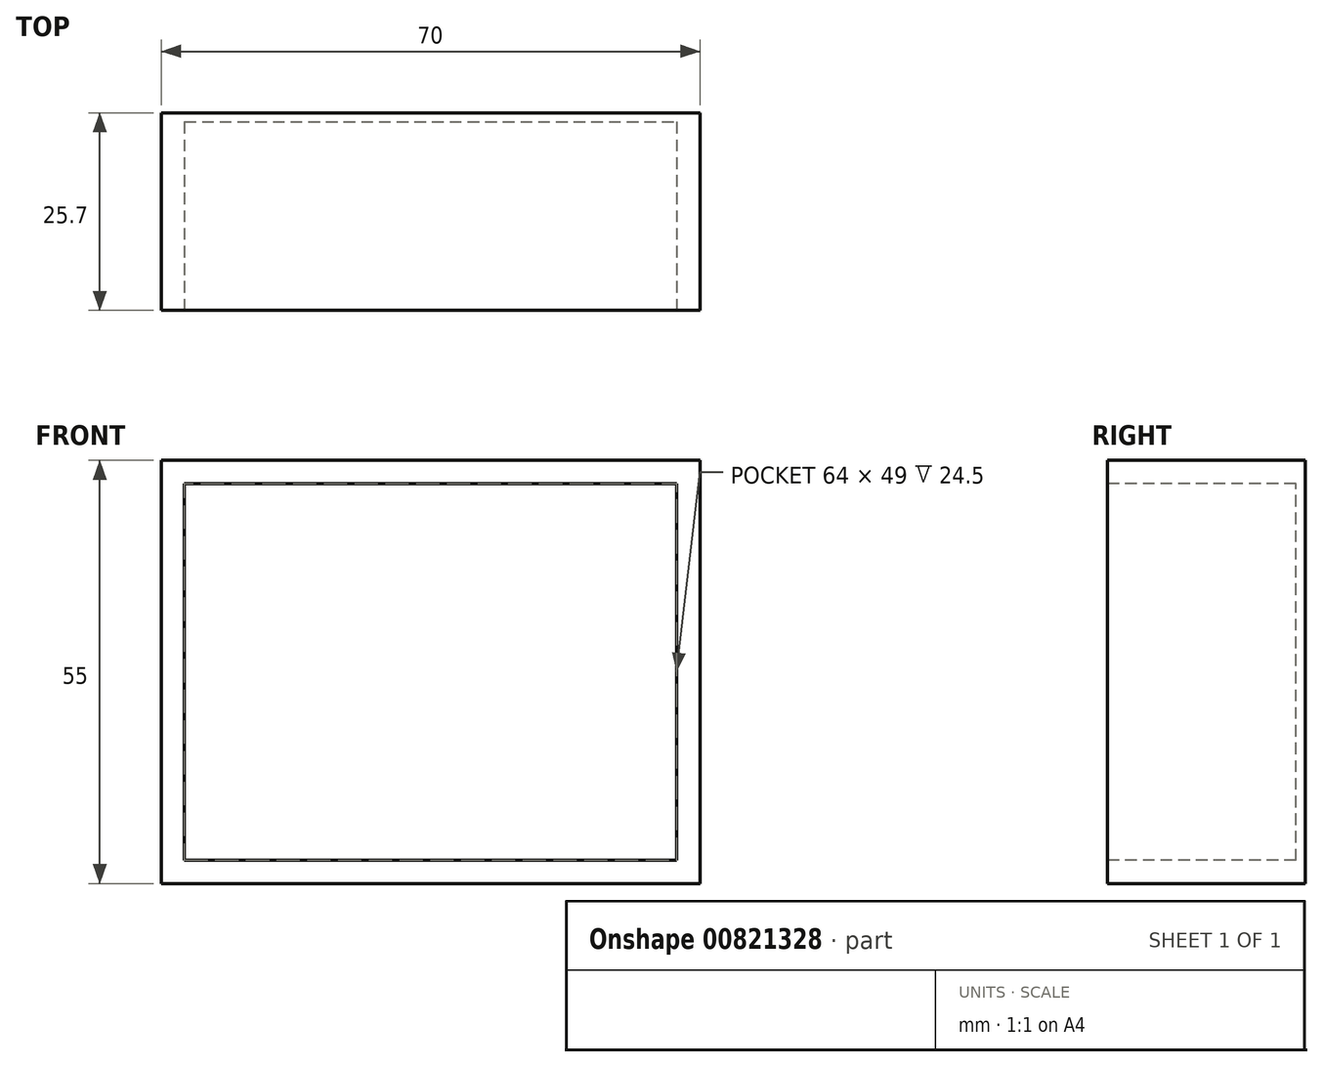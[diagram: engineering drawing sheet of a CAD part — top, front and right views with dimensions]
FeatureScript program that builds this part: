
annotation { "Feature Type Name" : "Feature", "Feature Type Description" : "" }
export const myFeature = defineFeature(function(context is Context, id is Id, definition is map)
    precondition{}
    {
        {
            var Q0;
            Q0=qCreatedBy(makeId("Front.planeOp"),FACE);
            var sketch = newSketch(context, id + "F0", { "sketchPlane" : qUnion([Q0])});
            skLineSegment(sketch, "E0.bottom", {"start": v(0, 0) * mm, "end": v(70, 0) * mm});
            skLineSegment(sketch, "E0.top", {"start": v(0, 55) * mm, "end": v(70, 55) * mm});
            skLineSegment(sketch, "E0.left", {"start": v(0, 0) * mm, "end": v(0, 55) * mm});
            skLineSegment(sketch, "E0.right", {"start": v(70, 0) * mm, "end": v(70, 55) * mm});
            skSolve(sketch);
        }
        {
            var Q0;
            Q0=makeQuery(id+"F0.imprint","IMPRINT",FACE,{"disambiguationData":[TD([[makeQuery(id+"F0.imprint","IMPRINT",EDGE,{"derivedFrom":sQuery(id+"F0.wireOp",EDGE,"E0.bottom")}),1.0]])]});
            extrude(context, id + "F1", {"entities" : qUnion([Q0]), "depth" : 25.7 * mm, "offsetDistance" : 25 * mm});
        }
        {
            var Q0;
            Q0=makeQuery(id+"F1.opExtrude","CAP_FACE",FACE,{"disambiguationData":[OSD([sQuery(id+"F0.wireOp",EDGE,"E0.bottom"),sQuery(id+"F0.wireOp",EDGE,"E0.top"),sQuery(id+"F0.wireOp",EDGE,"E0.left"),sQuery(id+"F0.wireOp",EDGE,"E0.right")])],"isStart":false});
            var sketch = newSketch(context, id + "F2", { "sketchPlane" : qUnion([Q0])});
            skLineSegment(sketch, "E1.0", {"start": v(3, 52) * mm, "end": v(67, 52) * mm});
            skLineSegment(sketch, "E1.1", {"start": v(3, 3) * mm, "end": v(3, 52) * mm});
            skLineSegment(sketch, "E1.2", {"start": v(3, 3) * mm, "end": v(67, 3) * mm});
            skLineSegment(sketch, "E1.3", {"start": v(67, 3) * mm, "end": v(67, 52) * mm});
            skSolve(sketch);
        }
        {
            var Q0;
            Q0 = qSketchRegion(id + "F2", true);
            extrude(context, id + "F3", {"entities" : qUnion([Q0]), "operationType" : NewBodyOperationType.REMOVE, "oppositeDirection" : true, "depth" : 24.5 * mm, "offsetDistance" : 25 * mm});
        }
    });
